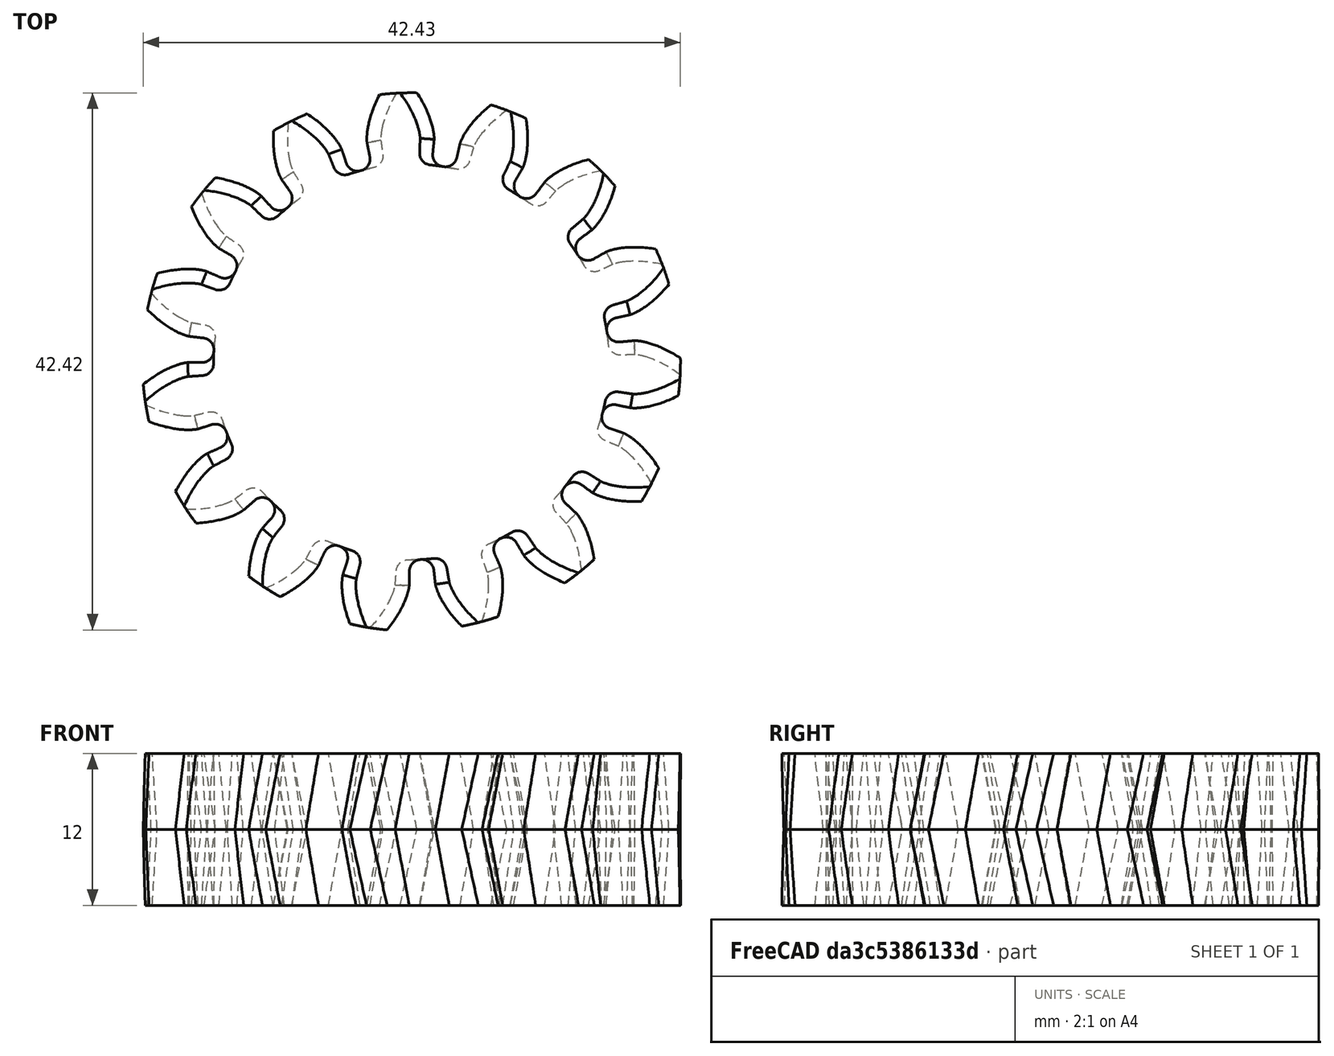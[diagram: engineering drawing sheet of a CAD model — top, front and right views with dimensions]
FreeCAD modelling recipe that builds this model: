
FCSTD DOCUMENT  (FreeCAD 0.16R6707 (Git))
Label: Engranaje_2
License: All rights reserved
LicenseURL: http://en.wikipedia.org/wiki/All_rights_reserved
objects: Part::Part2DObjectPython×2, Part::Helix×2, Part::Sweep×2
note: 6 computed .brp shape members not serialized (recipe doc carries the construction recipe); baked Part::Feature solids carry a one-line shape summary decoded from their .brp

FEATURE [Part::Part2DObjectPython] InvoluteGear  # Draft 2D object (typed FeaturePython)
  ExternalGear = true
  HighPrecision = true
  Modules = 2.5
  NumberOfTeeth = 15
  PressureAngle = 20
FEATURE [Part::Helix] Helix  label="Dientes_Dch"
  Angle = 0
  Height = 6
  LocalCoord = 0
  Pitch = 600
  Radius = 1
  Style = 1
FEATURE [Part::Sweep] Sweep  label="Engranaje_Dch"
  Frenet = true
  Placement = pos=(0,0,6) rot=(0,0,-1;0.087266rad)
  Sections = -> [InvoluteGear]
  Solid = true
  Spine = -> Helix [Edge1]
  Transition = 1
FEATURE [Part::Part2DObjectPython] InvoluteGear001  # Draft 2D object (typed FeaturePython)
  ExternalGear = true
  HighPrecision = true
  Modules = 2.5
  NumberOfTeeth = 15
  PressureAngle = 20
FEATURE [Part::Helix] Helix001  label="Espiral"
  Angle = 0
  Height = 6
  LocalCoord = 1
  Pitch = 600
  Radius = 1
  Style = 1
FEATURE [Part::Sweep] Sweep001
  Frenet = true
  Placement = pos=(0,0,0) rot=(0,0,-1;0.024435rad)
  Sections = -> [InvoluteGear001]
  Solid = true
  Spine = -> Helix001 [Edge1]
  Transition = 1
